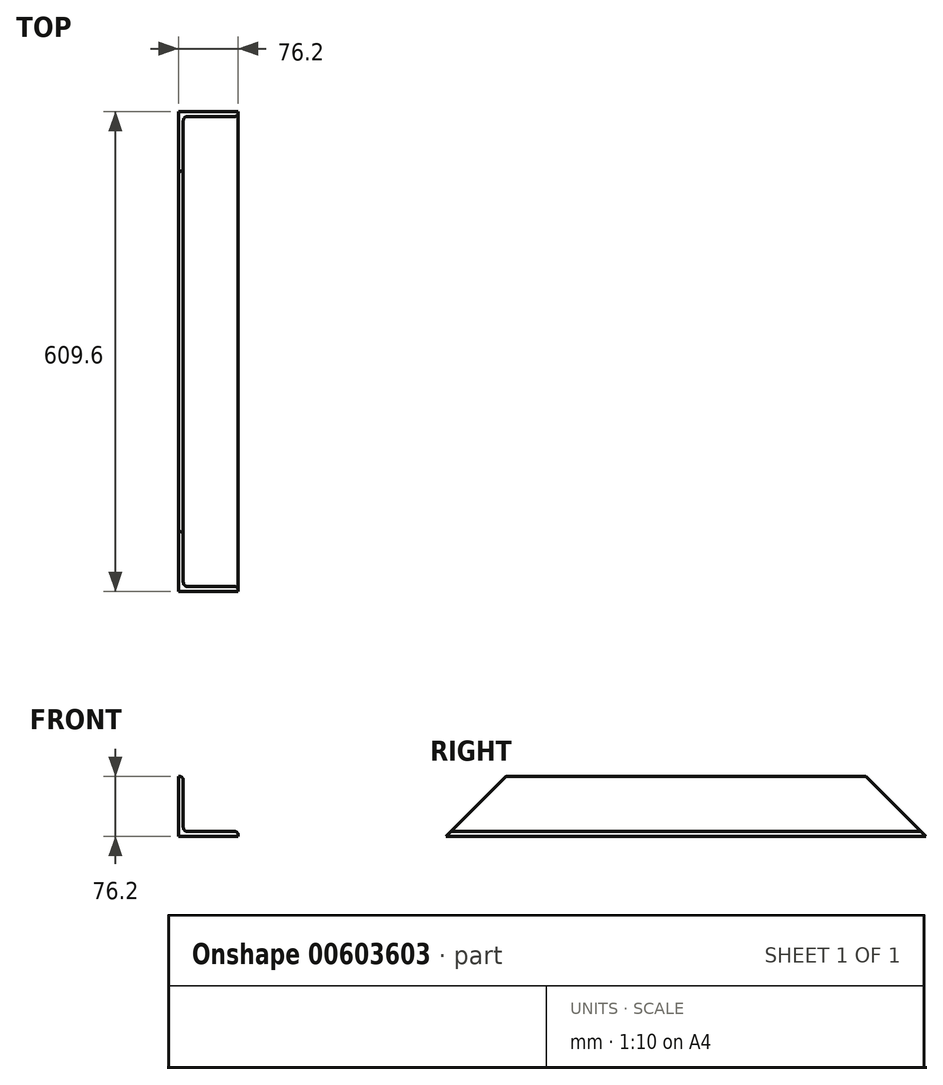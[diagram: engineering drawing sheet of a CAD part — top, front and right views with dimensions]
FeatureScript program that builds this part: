
annotation { "Feature Type Name" : "Feature", "Feature Type Description" : "" }
export const myFeature = defineFeature(function(context is Context, id is Id, definition is map)
    precondition{}
    {
        {
            var Q0;
            Q0=qCreatedBy(makeId("Front.planeOp"),FACE);
            var sketch = newSketch(context, id + "F0", { "sketchPlane" : qUnion([Q0])});
            skLineSegment(sketch, "E0.bottom", {"start": v(38.1, -38.1) * mm, "end": v(-38.1, -38.1) * mm});
            skLineSegment(sketch, "E0.top", {"start": v(-31.75, 38.1) * mm, "end": v(-38.1, 38.1) * mm});
            skLineSegment(sketch, "E0.left", {"start": v(38.1, -38.1) * mm, "end": v(38.1, -31.75) * mm});
            skLineSegment(sketch, "E0.right", {"start": v(-38.1, -38.1) * mm, "end": v(-38.1, 38.1) * mm});
            skPoint(sketch, "E0.middle", {"position": v(0, 0) * mm});
            skLineSegment(sketch, "E1.0", {"start": v(-31.75, -31.75) * mm, "end": v(-31.75, 38.1) * mm});
            skLineSegment(sketch, "E2.0", {"start": v(38.1, -31.75) * mm, "end": v(-31.75, -31.75) * mm});
            skPoint(sketch, "E3.orphan", {"position": v(38.1, 38.1) * mm});
            skSolve(sketch);
        }
        {
            var Q0;
            Q0 = qSketchRegion(id + "F0", true);
            extrude(context, id + "F1", {"entities" : qUnion([Q0]), "endBound" : BoundingType.SYMMETRIC, "depth" : 609.6 * mm, "offsetDistance" : 25.4 * mm});
        }
        {
            var Q0;
            Q0=makeQuery(id+"F1.opExtrude","SWEPT_EDGE",EDGE,{"disambiguationData":[OSD([sQuery(id+"F0.wireOp",EDGE,"E0.top"),sQuery(id+"F0.wireOp",EDGE,"E1.0")])]});
            var Q1;
            Q1=makeQuery(id+"F1.opExtrude","SWEPT_EDGE",EDGE,{"disambiguationData":[OSD([sQuery(id+"F0.wireOp",EDGE,"E1.0"),sQuery(id+"F0.wireOp",EDGE,"E2.0")])]});
            var Q2;
            Q2=makeQuery(id+"F1.opExtrude","SWEPT_EDGE",EDGE,{"disambiguationData":[OSD([sQuery(id+"F0.wireOp",EDGE,"E0.left"),sQuery(id+"F0.wireOp",EDGE,"E2.0")])]});
            fillet(context, id + "F2", {"entities" : qUnion([Q0, Q1, Q2]), "radius" : 5.08 * mm, "tangentPropagation" : true, "allowEdgeOverflow" : false});
        }
        {
            var Q0;
            Q0=makeQuery(id+"F1.opExtrude","SWEPT_FACE",FACE,{"disambiguationData":[OSD([sQuery(id+"F0.wireOp",EDGE,"E0.right")])]});
            var sketch = newSketch(context, id + "F3", { "sketchPlane" : qUnion([Q0])});
            skLineSegment(sketch, "E4", {"start": v(-304.8, -38.1) * mm, "end": v(-228.6, 38.1) * mm});
            skLineSegment(sketch, "E5", {"start": v(-228.6, 38.1) * mm, "end": v(-304.8, 38.1) * mm});
            skLineSegment(sketch, "E6", {"start": v(-304.8, 38.1) * mm, "end": v(-304.8, -38.1) * mm});
            skLineSegment(sketch, "E7.MirrorCS", {"start": v(304.8, -38.1) * mm, "end": v(228.6, 38.1) * mm});
            skLineSegment(sketch, "E8.MirrorCS", {"start": v(228.6, 38.1) * mm, "end": v(304.8, 38.1) * mm});
            skLineSegment(sketch, "E9.MirrorCS", {"start": v(304.8, 38.1) * mm, "end": v(304.8, -38.1) * mm});
            skSolve(sketch);
        }
        {
            var Q0;
            Q0 = qSketchRegion(id + "F3", true);
            extrude(context, id + "F4", {"entities" : qUnion([Q0]), "operationType" : NewBodyOperationType.REMOVE, "oppositeDirection" : true, "depth" : 76.2 * mm, "offsetDistance" : 25.4 * mm});
        }
    });
